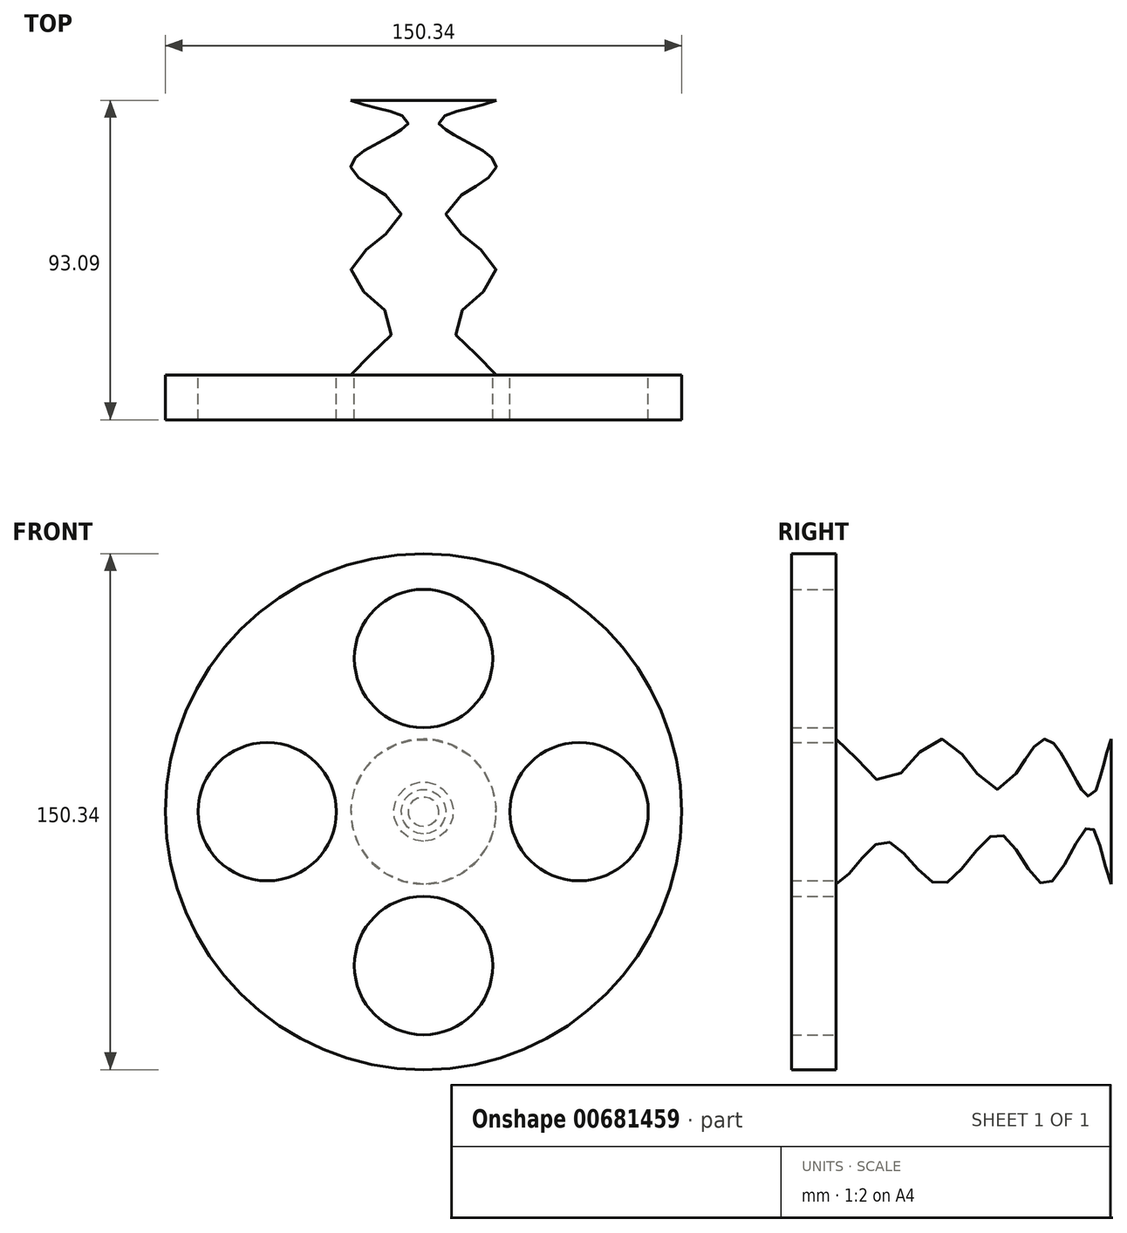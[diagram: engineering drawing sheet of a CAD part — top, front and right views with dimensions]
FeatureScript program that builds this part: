
annotation { "Feature Type Name" : "Feature", "Feature Type Description" : "" }
export const myFeature = defineFeature(function(context is Context, id is Id, definition is map)
    precondition{}
    {
        {
            var Q0;
            Q0=qCreatedBy(makeId("Front.planeOp"),FACE);
            var sketch = newSketch(context, id + "F0", { "sketchPlane" : qUnion([Q0])});
            skCircle(sketch, "E0", {"center": v(0, 0) * mm, "radius": 75.17 * mm});
            skCircle(sketch, "E1", {"center": v(-45.55, 0) * mm, "radius": 20.15 * mm});
            skCircle(sketch, "E2", {"center": v(0, 44.63) * mm, "radius": 20.15 * mm});
            skCircle(sketch, "E3", {"center": v(45.32, 0) * mm, "radius": 20.15 * mm});
            skCircle(sketch, "E4", {"center": v(0, -44.86) * mm, "radius": 20.15 * mm});
            skSolve(sketch);
        }
        {
            var Q0;
            Q0=makeQuery(id+"F0.imprint","IMPRINT",FACE,{"disambiguationData":[TD([[makeQuery(id+"F0.imprint","IMPRINT",EDGE,{"derivedFrom":sQuery(id+"F0.wireOp",EDGE,"E0")}),1.0]])]});
            var Q1;
            Q1 = qSketchRegion(id + "F2", true);
            extrude(context, id + "F1", {"entities" : qUnion([Q0, Q1]), "depth" : 13 * mm, "offsetDistance" : 25 * mm});
        }
        {
            var Q0;
            Q0=qCreatedBy(makeId("Top.planeOp"),FACE);
            var sketch = newSketch(context, id + "F2", { "sketchPlane" : qUnion([Q0])});
            skLineSegment(sketch, "E5", {"start": v(0, 0) * mm, "end": v(0, 80.1) * mm});
            skLineSegment(sketch, "E6", {"start": v(0, 0) * mm, "end": v(-21.16, 0) * mm});
            skFitSpline(sketch, "E7", {"points": [v(-21.16, 0) * mm, v(-8.64, 14.5) * mm, v(-21.16, 30.6) * mm, v(-6.5, 47.4) * mm, v(-21.16, 61.13) * mm, v(-4.38, 73.67) * mm, v(-21.16, 80.1) * mm], "startDerivative": vector(34.86, 85.2) * mm, "endDerivative": vector(-85.97, 40.08) * mm});
            skLineSegment(sketch, "E8", {"start": v(0, 80.1) * mm, "end": v(-21.16, 80.1) * mm});
            skSolve(sketch);
        }
        {
            var Q0;
            Q0=makeQuery(id+"F2.imprint","IMPRINT",FACE,{"disambiguationData":[TD([[makeQuery(id+"F2.imprint","IMPRINT",EDGE,{"derivedFrom":sQuery(id+"F2.wireOp",EDGE,"E5")}),1.0]])]});
            var Q1;
            Q1=sQuery(id+"F2.wireOp",EDGE,"E5");
            revolve(context, id + "F3", {"operationType" : NewBodyOperationType.ADD, "entities" : qUnion([Q0]), "axis" : qUnion([Q1]), "revolveType" : RevolveType.FULL});
        }
        {
            var Q0;
            Q0=qCreatedBy(makeId("Top.planeOp"),FACE);
            var sketch = newSketch(context, id + "F4", { "sketchPlane" : qUnion([Q0])});
            skLineSegment(sketch, "E9", {"start": v(0, 80.1) * mm, "end": v(0, 93.3) * mm});
            skLineSegment(sketch, "E10", {"start": v(-21.34, 80.1) * mm, "end": v(0, 80.1) * mm});
            skLineSegment(sketch, "E11", {"start": v(-21.34, 80.1) * mm, "end": v(-21.34, 93.25) * mm});
            skLineSegment(sketch, "E12", {"start": v(-21.34, 93.25) * mm, "end": v(0, 93.3) * mm});
            skSolve(sketch);
        }
        {
            var Q0;
            Q0=makeQuery(id+"F4.imprint","IMPRINT",FACE,{"disambiguationData":[TD([[makeQuery(id+"F4.imprint","IMPRINT",EDGE,{"derivedFrom":sQuery(id+"F4.wireOp",EDGE,"E9")}),1.0]])]});
            var Q1;
            Q1=sQuery(id+"F4.wireOp",EDGE,"E12");
            var Q2;
            Q2=sQuery(id+"F4.wireOp",EDGE,"E11");
            var Q3;
            Q3=sQuery(id+"F4.wireOp",EDGE,"E9");
            revolve(context, id + "F5", {"bodyType" : ToolBodyType.SURFACE, "entities" : qUnion([Q0]), "surfaceEntities" : qUnion([Q1, Q2]), "axis" : qUnion([Q3]), "revolveType" : RevolveType.FULL});
        }
    });
